# Revit family: SP-AU
name_source: partatom
category: Устройства связи
revit_build: Autodesk Revit 2016 (Build: 20160314_0715(x64)
units: mm (PartAtom-declared; Revit-internal decimal feet)

## family parameters
Всегда вертикально = Нет
На основе рабочей плоскости = Да
Общий = Да
При загрузке вырезать с полостями = Нет
Размер круглого соединителя = Использовать диаметр
Сохранять ориентацию аннотаций = Нет
Тип детали = Нормальный
Точка расчета площади = Нет

## types (2) — shared parameters
ADSK_URL страницы изделия = https://www.bas-ip.ru
ADSK_Версия Revit = Revit 2016
ADSK_Единица измерения = шт
ADSK_Завод-изготовитель = BAS-IP
ADSK_Наименование = SIP ТРУБКА SP-02P
ADSK_Размер_Длина = 50 мм
ADSK_Размер_Толщина = 50 мм
ADSK_Размер_Ширина = 185 мм
BIM library = https://bimlib.ru
URL = https://www.bas-ip.ru
Группа модели = Трубка
Изготовитель = BAS-IP
Изображение типоразмера = <Нет>
Описание = Дополнительная аудиотрубка, которая подключается непосредственно к домофону AU-04L. Это решение идеально подходит для тех, кто желает конфиденциальности в разговорах.
Размер = 185x60 мм
zero-valued in all types: Отметка по умолчанию

## per-type parameters (varying)
| type | Материал корпуса | Цвет |
| SP-AU BLACK | SHV_Черный пластик | Черный |
| SP-AU WHITE | SHV_Белый пластик | Белый |

note: column(s) folded — value = type name in every type: ADSK_Марка, ADSK_Наименование краткое
